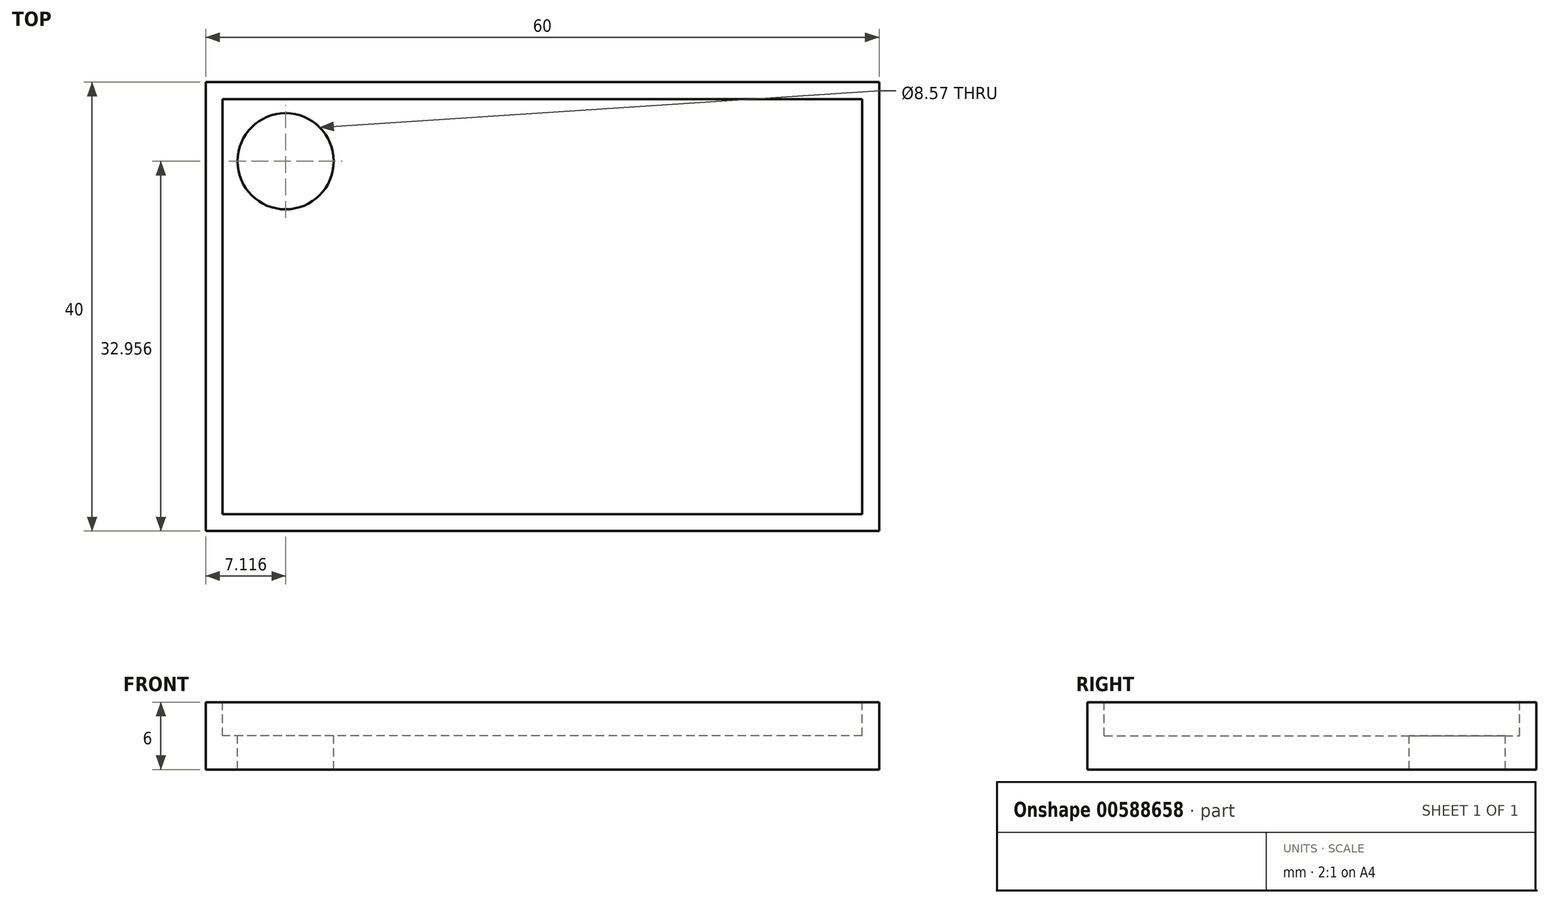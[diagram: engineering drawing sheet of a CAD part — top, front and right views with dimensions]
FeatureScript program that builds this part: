
annotation { "Feature Type Name" : "Feature", "Feature Type Description" : "" }
export const myFeature = defineFeature(function(context is Context, id is Id, definition is map)
    precondition{}
    {
        {
            var Q0;
            Q0=qCreatedBy(makeId("Top.planeOp"),FACE);
            var sketch = newSketch(context, id + "F0", { "sketchPlane" : qUnion([Q0])});
            skLineSegment(sketch, "E0.bottom", {"start": v(30, -20) * mm, "end": v(-30, -20) * mm});
            skLineSegment(sketch, "E0.top", {"start": v(30, 20) * mm, "end": v(-30, 20) * mm});
            skLineSegment(sketch, "E0.left", {"start": v(30, -20) * mm, "end": v(30, 20) * mm});
            skLineSegment(sketch, "E0.right", {"start": v(-30, -20) * mm, "end": v(-30, 20) * mm});
            skPoint(sketch, "E0.middle", {"position": v(0, 0) * mm});
            skSolve(sketch);
        }
        {
            var Q0;
            Q0=makeQuery(id+"F0.imprint","IMPRINT",FACE,{"disambiguationData":[TD([[makeQuery(id+"F0.imprint","IMPRINT",EDGE,{"derivedFrom":sQuery(id+"F0.wireOp",EDGE,"E0.bottom")}),-1.0]])]});
            extrude(context, id + "F1", {"entities" : qUnion([Q0]), "endBound" : BoundingType.SYMMETRIC, "depth" : 6 * mm, "offsetDistance" : 25 * mm});
        }
        {
            var Q0;
            Q0=makeQuery(id+"F1.opExtrude","CAP_FACE",FACE,{"disambiguationData":[OSD([sQuery(id+"F0.wireOp",EDGE,"E0.bottom"),sQuery(id+"F0.wireOp",EDGE,"E0.top"),sQuery(id+"F0.wireOp",EDGE,"E0.left"),sQuery(id+"F0.wireOp",EDGE,"E0.right")])],"isStart":false});
            var sketch = newSketch(context, id + "F2", { "sketchPlane" : qUnion([Q0])});
            skLineSegment(sketch, "E1.bottom", {"start": v(28.5, -18.5) * mm, "end": v(-28.5, -18.5) * mm});
            skLineSegment(sketch, "E1.top", {"start": v(28.5, 18.5) * mm, "end": v(-28.5, 18.5) * mm});
            skLineSegment(sketch, "E1.left", {"start": v(28.5, -18.5) * mm, "end": v(28.5, 18.5) * mm});
            skLineSegment(sketch, "E1.right", {"start": v(-28.5, -18.5) * mm, "end": v(-28.5, 18.5) * mm});
            skPoint(sketch, "E1.middle", {"position": v(0, 0) * mm});
            skSolve(sketch);
        }
        {
            var Q0;
            Q0 = qSketchRegion(id + "F2", true);
            extrude(context, id + "F3", {"entities" : qUnion([Q0]), "operationType" : NewBodyOperationType.REMOVE, "oppositeDirection" : true, "depth" : 3 * mm, "offsetDistance" : 25 * mm});
        }
        {
            var Q0;
            Q0=makeQuery(id+"F3.boolean.opBoolean","COPY",FACE,{"derivedFrom":makeQuery(id+"F3.opExtrude","CAP_FACE",FACE,{"disambiguationData":[OSD([sQuery(id+"F2.wireOp",EDGE,"E1.bottom"),sQuery(id+"F2.wireOp",EDGE,"E1.top"),sQuery(id+"F2.wireOp",EDGE,"E1.left"),sQuery(id+"F2.wireOp",EDGE,"E1.right")])],"isStart":false})});
            var sketch = newSketch(context, id + "F4", { "sketchPlane" : qUnion([Q0])});
            skText(sketch, "E2", { "text": "alanah", "fontName": "OpenSans-Regular.ttf"});
            const initialGuessF4  = {"E2": [-0.0285, -0.00472, 1, 0, 0.01312]};
            skSetInitialGuess(sketch, initialGuessF4);
            skSolve(sketch);
        }
        {
            var Q0;
            Q0 = qSketchRegion(id + "F4", true);
            var Q1;
            Q1 = qConstructionFilter(qBodyType(qCreatedBy(id + "F4" ,EDGE), BodyType.WIRE), ConstructionObject.NO);
            extrude(context, id + "F5", {"entities" : qUnion([Q0]), "bodyType" : ToolBodyType.SURFACE, "operationType" : NewBodyOperationType.ADD, "surfaceEntities" : qUnion([Q1]), "oppositeDirection" : true, "depth" : 4 * mm, "offsetDistance" : 25 * mm});
        }
        {
            var Q0;
            {var subQ0=sQuery(id+"F2.wireOp",EDGE,"E1.left");var subQ1=sQuery(id+"F2.wireOp",EDGE,"E1.top");var subQ2=sQuery(id+"F2.wireOp",EDGE,"E1.bottom");var subQ3=sQuery(id+"F2.wireOp",EDGE,"E1.right");Q0=makeQuery(id+"F5.boolean.opBoolean","SPLIT",FACE,{"disambiguationData":[TD([makeQuery(id+"F3.boolean.opBoolean","COPY",FACE,{"derivedFrom":makeQuery(id+"F3.opExtrude","SWEPT_FACE",FACE,{"disambiguationData":[OSD([subQ2])]})})])],"derivedFrom":makeQuery(id+"F3.boolean.opBoolean","COPY",FACE,{"derivedFrom":makeQuery(id+"F3.opExtrude","CAP_FACE",FACE,{"disambiguationData":[OSD([subQ2,subQ1,subQ0,subQ3])],"isStart":false})})});}
            var sketch = newSketch(context, id + "F6", { "sketchPlane" : qUnion([Q0])});
            skCircle(sketch, "E3", {"center": v(-22.88, 12.96) * mm, "radius": 4.28 * mm});
            skSolve(sketch);
        }
        {
            var Q0;
            Q0=makeQuery(id+"F6.imprint","IMPRINT",FACE,{"disambiguationData":[TD([[makeQuery(id+"F6.imprint","IMPRINT",EDGE,{"derivedFrom":sQuery(id+"F6.wireOp",EDGE,"E3")}),1.0]])]});
            extrude(context, id + "F7", {"entities" : qUnion([Q0]), "operationType" : NewBodyOperationType.REMOVE, "oppositeDirection" : true, "depth" : 6 * mm, "offsetDistance" : 25 * mm});
        }
    });
